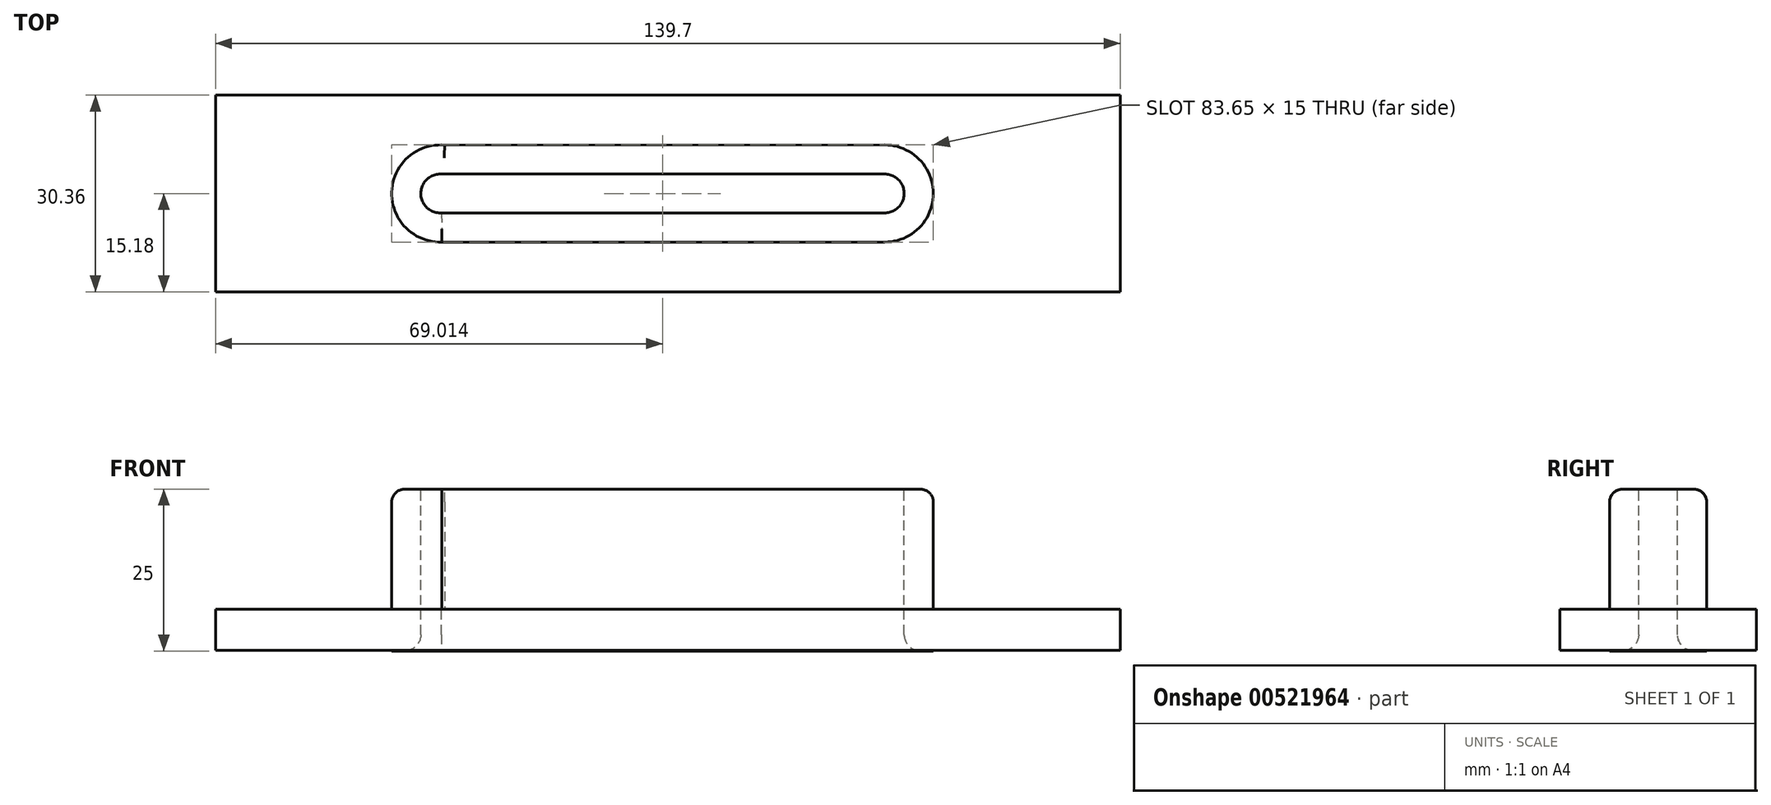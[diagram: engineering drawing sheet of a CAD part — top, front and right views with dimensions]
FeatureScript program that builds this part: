
annotation { "Feature Type Name" : "Feature", "Feature Type Description" : "" }
export const myFeature = defineFeature(function(context is Context, id is Id, definition is map)
    precondition{}
    {
        {
            var Q0;
            Q0=qCreatedBy(makeId("Top.planeOp"),FACE);
            var sketch = newSketch(context, id + "F0", { "sketchPlane" : qUnion([Q0])});
            skCircle(sketch, "E0", {"center": v(-35.16, 0) * mm, "radius": 7.5 * mm});
            skCircle(sketch, "E1", {"center": v(33.49, 0) * mm, "radius": 7.5 * mm});
            skLineSegment(sketch, "E2", {"start": v(-35.87, 7.47) * mm, "end": v(33.48, 7.5) * mm});
            skLineSegment(sketch, "E3", {"start": v(-35.42, -7.5) * mm, "end": v(33.49, -7.5) * mm});
            skSolve(sketch);
        }
        {
            var Q0;
            Q0 = qSketchRegion(id + "F0", true);
            extrude(context, id + "F1", {"entities" : qUnion([Q0]), "depth" : 25 * mm, "offsetDistance" : 25 * mm});
        }
        {
            var Q0;
            Q0=makeQuery(id+"F1.opExtrude","CAP_FACE",FACE,{"disambiguationData":[OSD([sQuery(id+"F0.wireOp",EDGE,"E0"),sQuery(id+"F0.wireOp",EDGE,"E1"),sQuery(id+"F0.wireOp",EDGE,"E2"),sQuery(id+"F0.wireOp",EDGE,"E3")])],"isStart":false});
            cPlane(context, id + "F2", {"entities" : qUnion([Q0]), "cplaneType" : CPlaneType.OFFSET, "offset" : 24.92 * mm, "oppositeDirection" : true, "width" : 150 * mm, "height" : 150 * mm});
        }
        {
            var Q0;
            Q0=makeQuery(id+"F1.opExtrude","CAP_FACE",FACE,{"disambiguationData":[OSD([sQuery(id+"F0.wireOp",EDGE,"E0"),sQuery(id+"F0.wireOp",EDGE,"E1"),sQuery(id+"F0.wireOp",EDGE,"E2"),sQuery(id+"F0.wireOp",EDGE,"E3")])],"isStart":false});
            var sketch = newSketch(context, id + "F3", { "sketchPlane" : qUnion([Q0])});
            skCircle(sketch, "E4", {"center": v(-35.16, 0) * mm, "radius": 3 * mm});
            skCircle(sketch, "E5", {"center": v(33.48, 0) * mm, "radius": 3 * mm});
            skPoint(sketch, "E5.centerSnap0", {"position": v(40.99, 0) * mm});
            skLineSegment(sketch, "E6", {"start": v(-35.16, 3) * mm, "end": v(33.48, 3) * mm});
            skLineSegment(sketch, "E7", {"start": v(-34.97, -3) * mm, "end": v(33.48, -3) * mm});
            skSolve(sketch);
        }
        {
            var Q0;
            Q0=makeQuery(id+"F1.opExtrude","CAP_FACE",FACE,{"disambiguationData":[OSD([sQuery(id+"F0.wireOp",EDGE,"E0"),sQuery(id+"F0.wireOp",EDGE,"E1"),sQuery(id+"F0.wireOp",EDGE,"E2"),sQuery(id+"F0.wireOp",EDGE,"E3")])],"isStart":false});
            fillet(context, id + "F4", {"entities" : qUnion([Q0]), "radius" : 2 * mm, "tangentPropagation" : true, "allowEdgeOverflow" : false});
        }
        {
            var Q0;
            Q0=qCreatedBy(id+"F2.planeOp",FACE);
            var sketch = newSketch(context, id + "F5", { "sketchPlane" : qUnion([Q0])});
            skLineSegment(sketch, "E8.bottom", {"start": v(69.85, -15.18) * mm, "end": v(-69.85, -15.18) * mm});
            skLineSegment(sketch, "E8.top", {"start": v(69.85, 15.18) * mm, "end": v(-69.85, 15.18) * mm});
            skLineSegment(sketch, "E8.left", {"start": v(69.85, -15.18) * mm, "end": v(69.85, 15.18) * mm});
            skLineSegment(sketch, "E8.right", {"start": v(-69.85, -15.18) * mm, "end": v(-69.85, 15.18) * mm});
            skPoint(sketch, "E8.middle", {"position": v(0, 0) * mm});
            skSolve(sketch);
        }
        {
            var Q0;
            Q0=makeQuery(id+"F5.imprint","IMPRINT",FACE,{"disambiguationData":[TD([[makeQuery(id+"F5.imprint","IMPRINT",EDGE,{"derivedFrom":sQuery(id+"F5.wireOp",EDGE,"E8.bottom")}),-1.0]])]});
            extrude(context, id + "F6", {"entities" : qUnion([Q0]), "operationType" : NewBodyOperationType.ADD, "depth" : 6.35 * mm, "offsetDistance" : 25.4 * mm});
        }
        {
            var Q0;
            Q0 = qSketchRegion(id + "F3", true);
            extrude(context, id + "F7", {"entities" : qUnion([Q0]), "operationType" : NewBodyOperationType.REMOVE, "oppositeDirection" : true, "depth" : 25.4 * mm, "offsetDistance" : 25.4 * mm});
        }
        {
            var Q0;
            Q0=makeQuery(id+"F7.boolean.opBoolean","INTERSECT",EDGE,{"derivedFrom":[makeQuery(id+"F1.opExtrude","CAP_FACE",FACE,{"disambiguationData":[OSD([sQuery(id+"F0.wireOp",EDGE,"E0"),sQuery(id+"F0.wireOp",EDGE,"E1"),sQuery(id+"F0.wireOp",EDGE,"E2"),sQuery(id+"F0.wireOp",EDGE,"E3")])],"isStart":true}),makeQuery(id+"F7.opExtrude","SWEPT_FACE",FACE,{"disambiguationData":[OSD([sQuery(id+"F3.wireOp",EDGE,"E6")])]})]});
            fillet(context, id + "F8", {"entities" : qUnion([Q0]), "radius" : 2.54 * mm, "tangentPropagation" : true, "allowEdgeOverflow" : false});
        }
    });
